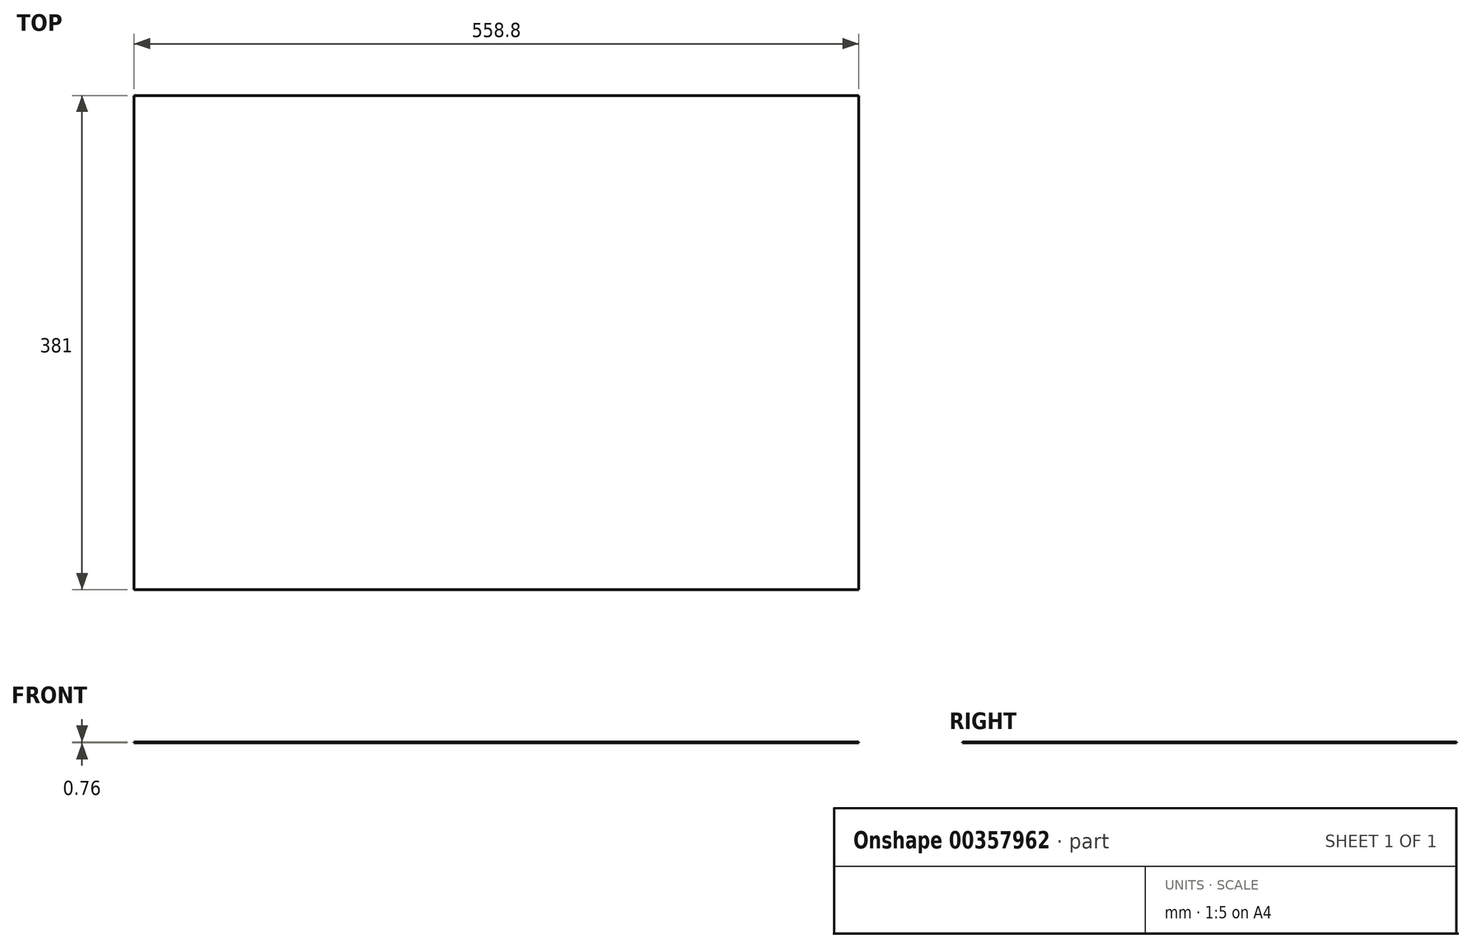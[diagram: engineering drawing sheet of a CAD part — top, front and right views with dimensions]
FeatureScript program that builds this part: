
annotation { "Feature Type Name" : "Feature", "Feature Type Description" : "" }
export const myFeature = defineFeature(function(context is Context, id is Id, definition is map)
    precondition{}
    {
        {
            var Q0;
            Q0=qCreatedBy(makeId("Top.planeOp"),FACE);
            var sketch = newSketch(context, id + "F0", { "sketchPlane" : qUnion([Q0])});
            skLineSegment(sketch, "E0.bottom", {"start": v(279.4, -190.5) * mm, "end": v(-279.4, -190.5) * mm});
            skLineSegment(sketch, "E0.top", {"start": v(279.4, 190.5) * mm, "end": v(-279.4, 190.5) * mm});
            skLineSegment(sketch, "E0.left", {"start": v(279.4, -190.5) * mm, "end": v(279.4, 190.5) * mm});
            skLineSegment(sketch, "E0.right", {"start": v(-279.4, -190.5) * mm, "end": v(-279.4, 190.5) * mm});
            skPoint(sketch, "E0.middle", {"position": v(0, 0) * mm});
            skSolve(sketch);
        }
        {
            var Q0;
            Q0=makeQuery(id+"F0.imprint","IMPRINT",FACE,{"disambiguationData":[TD([[makeQuery(id+"F0.imprint","IMPRINT",EDGE,{"derivedFrom":sQuery(id+"F0.wireOp",EDGE,"E0.bottom")}),-1.0]])]});
            extrude(context, id + "F1", {"entities" : qUnion([Q0]), "depth" : 0.76 * mm});
        }
    });
